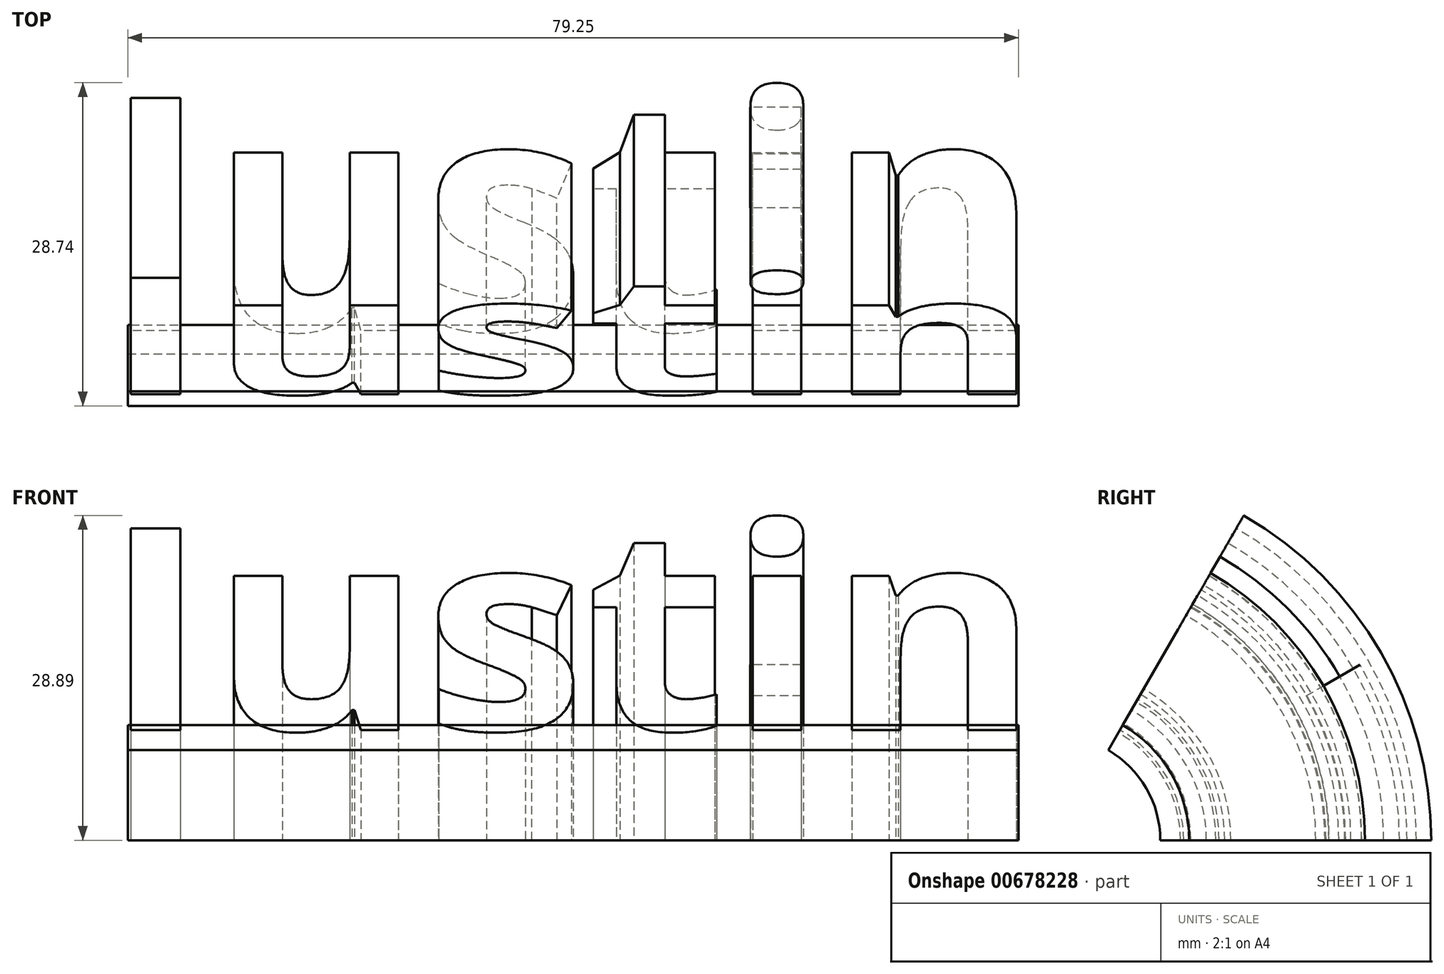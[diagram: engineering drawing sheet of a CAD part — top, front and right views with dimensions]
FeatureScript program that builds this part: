
annotation { "Feature Type Name" : "Feature", "Feature Type Description" : "" }
export const myFeature = defineFeature(function(context is Context, id is Id, definition is map)
    precondition{}
    {
        {
            var Q0;
            Q0=qCreatedBy(makeId("Top.planeOp"),FACE);
            var sketch = newSketch(context, id + "F0", { "sketchPlane" : qUnion([Q0])});
            skText(sketch, "E0", { "text": "Iustin", "fontName": "OpenSans-Bold.ttf"});
            const initialGuessF0  = {"E0": [0, 0.00208, 1, 0, 0.02088]};
            skSetInitialGuess(sketch, initialGuessF0);
            skSolve(sketch);
        }
        {
            var Q0;
            Q0=qCreatedBy(makeId("Top.planeOp"),FACE);
            var sketch = newSketch(context, id + "F1", { "sketchPlane" : qUnion([Q0])});
            skLineSegment(sketch, "E1.bottom", {"start": v(2.33, 2.58) * mm, "end": v(81.58, 2.58) * mm});
            skLineSegment(sketch, "E1.top", {"start": v(2.33, 0) * mm, "end": v(81.58, 0) * mm});
            skLineSegment(sketch, "E1.left", {"start": v(2.33, 2.58) * mm, "end": v(2.33, 0) * mm});
            skLineSegment(sketch, "E1.right", {"start": v(81.58, 2.58) * mm, "end": v(81.58, 0) * mm});
            skSolve(sketch);
        }
        {
            var Q0;
            Q0=qCreatedBy(makeId("Top.planeOp"),FACE);
            var sketch = newSketch(context, id + "F2", { "sketchPlane" : qUnion([Q0])});
            skLineSegment(sketch, "E2", {"start": v(0, -9.25) * mm, "end": v(133.4, -9.25) * mm});
            skSolve(sketch);
        }
        {
            var Q0;
            Q0 = qSketchRegion(id + "F0", true);
            var Q1;
            Q1 = qSketchRegion(id + "F1", true);
            var Q2;
            Q2=sQuery(id+"F2.wireOp",EDGE,"E2");
            revolve(context, id + "F3", {"entities" : qUnion([Q0, Q1]), "axis" : qUnion([Q2]), "revolveType" : RevolveType.ONE_DIRECTION, "angle" : 60 * degree});
        }
        {
            var Q0;
            Q0=qCreatedBy(makeId("Top.planeOp"),FACE);
            var sketch = newSketch(context, id + "F4", { "sketchPlane" : qUnion([Q0])});
            skLineSegment(sketch, "E3.bottom", {"start": v(62.25, 16.42) * mm, "end": v(57.73, 16.42) * mm});
            skLineSegment(sketch, "E3.top", {"start": v(62.25, 21.95) * mm, "end": v(57.73, 21.95) * mm});
            skLineSegment(sketch, "E3.left", {"start": v(62.25, 16.42) * mm, "end": v(62.25, 21.95) * mm});
            skLineSegment(sketch, "E3.right", {"start": v(57.73, 16.42) * mm, "end": v(57.73, 21.95) * mm});
            skSolve(sketch);
        }
        {
            var Q0;
            Q0 = qSketchRegion(id + "F4", true);
            var Q1;
            Q1=sQuery(id+"F2.wireOp",EDGE,"E2");
            revolve(context, id + "F5", {"entities" : qUnion([Q0]), "axis" : qUnion([Q1]), "revolveType" : RevolveType.ONE_DIRECTION, "angle" : 30 * degree});
        }
    });
